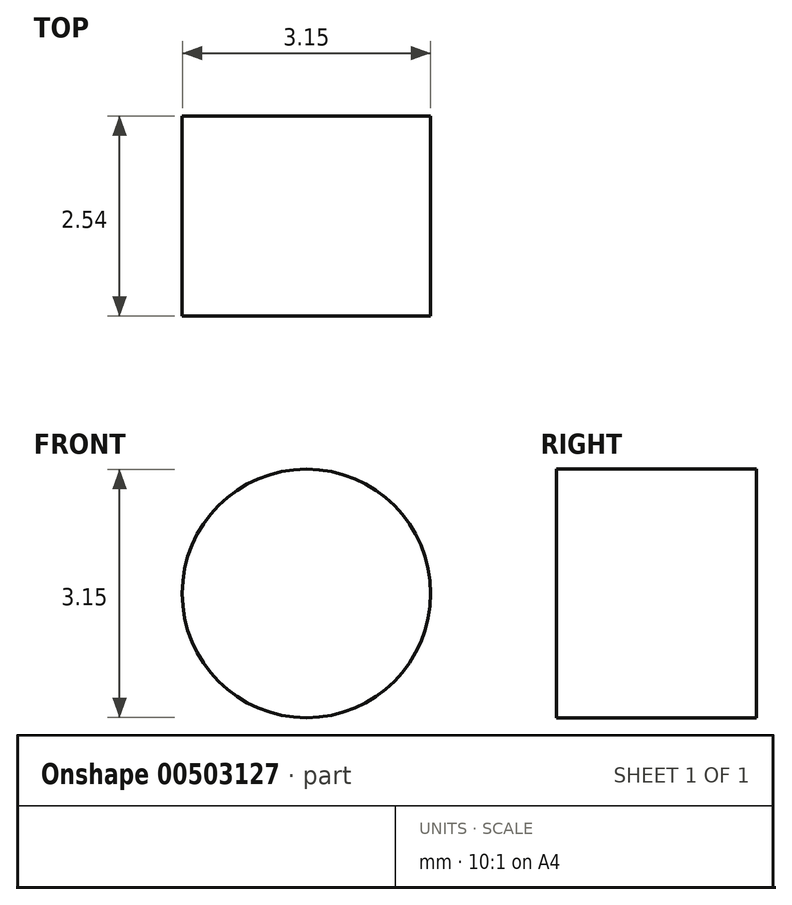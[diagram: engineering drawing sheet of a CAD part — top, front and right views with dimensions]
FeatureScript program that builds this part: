
annotation { "Feature Type Name" : "Feature", "Feature Type Description" : "" }
export const myFeature = defineFeature(function(context is Context, id is Id, definition is map)
    precondition{}
    {
        {
            var Q0;
            Q0=qCreatedBy(makeId("Front.planeOp"),FACE);
            var sketch = newSketch(context, id + "F0", { "sketchPlane" : qUnion([Q0])});
            skLineSegment(sketch, "E0", {"start": v(0, 74.54) * mm, "end": v(0, -28.9) * mm});
            skSolve(sketch);
        }
        {
            var Q0;
            Q0=qCreatedBy(makeId("Front.planeOp"),FACE);
            var sketch = newSketch(context, id + "F1", { "sketchPlane" : qUnion([Q0])});
            skCircle(sketch, "E1", {"center": v(-13.86, 64.57) * mm, "radius": 1.58 * mm});
            skSolve(sketch);
        }
        {
            var Q0;
            Q0=makeQuery(id+"F1.imprint","IMPRINT",FACE,{"disambiguationData":[TD([[makeQuery(id+"F1.imprint","IMPRINT",EDGE,{"derivedFrom":sQuery(id+"F1.wireOp",EDGE,"E1")}),1.0]])]});
            extrude(context, id + "F2", {"entities" : qUnion([Q0]), "depth" : 2.54 * mm});
        }
        {
            var Q0;
            Q0=qCreatedBy(makeId("Front.planeOp"),FACE);
            var sketch = newSketch(context, id + "F3", { "sketchPlane" : qUnion([Q0])});
            skFitSpline(sketch, "E2", {"points": [v(-17.39, 40.3) * mm, v(-12.24, 30.83) * mm, v(-16.7, 9.37) * mm, v(-9.73, -11.9) * mm, v(0, -14.47) * mm], "startDerivative": vector(35.66, -40.72) * mm, "endDerivative": vector(51.24, -0.64) * mm});
            skSolve(sketch);
        }
        {
            var Q0;
            Q0=sQuery(id+"F3.wireOp",EDGE,"E2");
            var Q1;
            Q1=sQuery(id+"F0.wireOp",EDGE,"E0");
            revolve(context, id + "F4", {"bodyType" : ToolBodyType.SURFACE, "surfaceEntities" : qUnion([Q0]), "axis" : qUnion([Q1]), "revolveType" : RevolveType.FULL});
        }
    });
